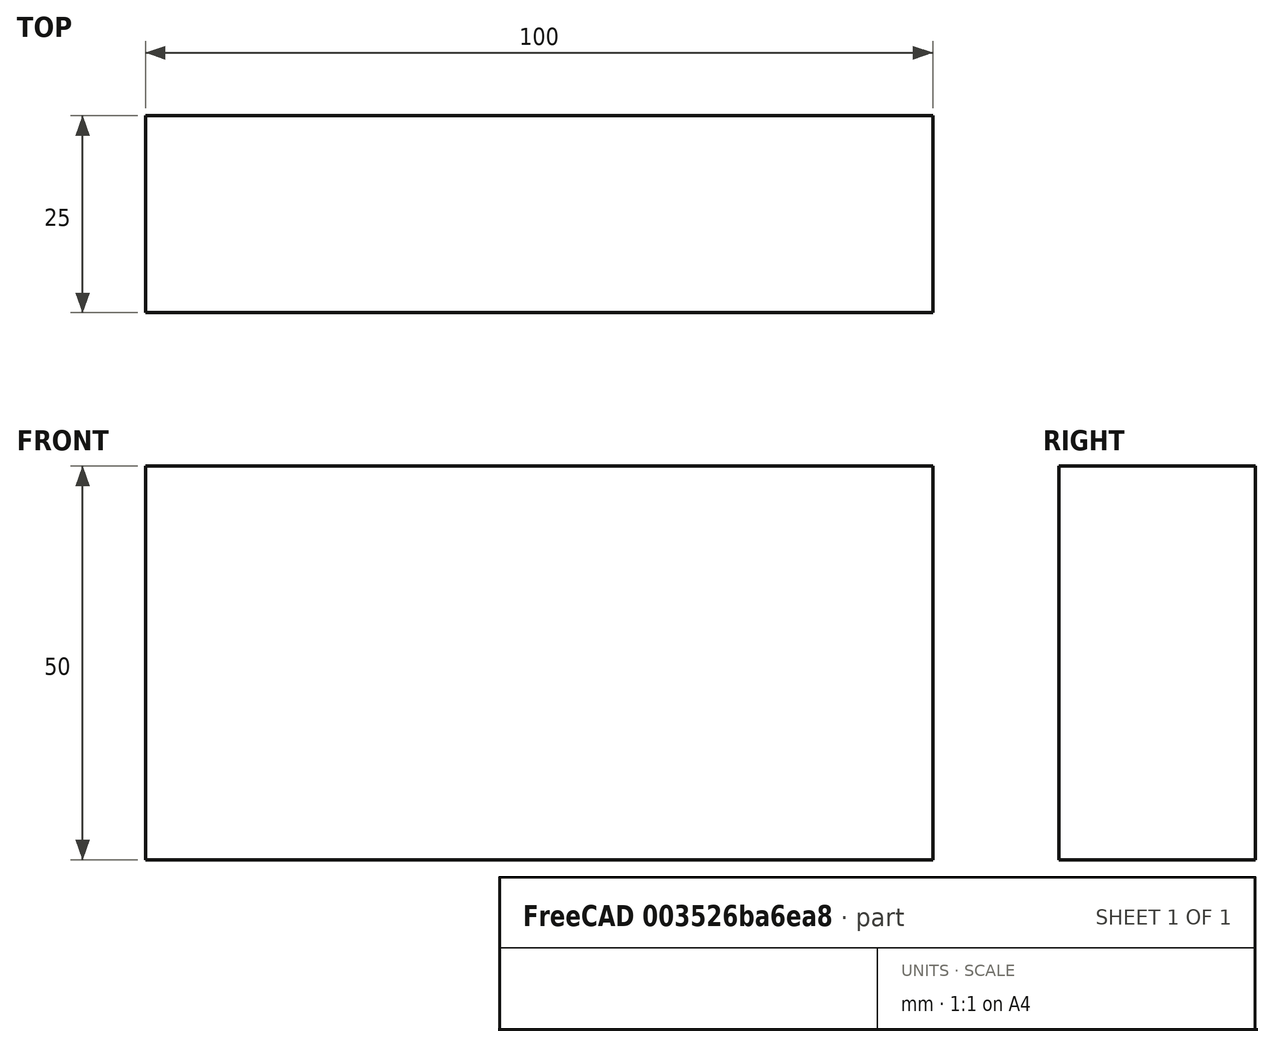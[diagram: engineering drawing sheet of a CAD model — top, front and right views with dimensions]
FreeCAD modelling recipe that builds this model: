
FCSTD DOCUMENT  (FreeCAD 0.15R4671 (Git))
Label: Flat Bar 100x25 EN10058 S235JR
License: All rights reserved
LicenseURL: http://en.wikipedia.org/wiki/All_rights_reserved
objects: Sketcher::SketchObject×1, Part::Extrusion×1
note: 2 computed .brp shape members not serialized (recipe doc carries the construction recipe); baked Part::Feature solids carry a one-line shape summary decoded from their .brp

FEATURE [Sketcher::SketchObject] Sketch
  sketch-geometry (4):
    g0: LineSegment StartX=-50 StartY=-12.5 StartZ=0 EndX=50 EndY=-12.5 EndZ=0
    g1: LineSegment StartX=50 StartY=-12.5 StartZ=0 EndX=50 EndY=12.5 EndZ=0
    g2: LineSegment StartX=50 StartY=12.5 StartZ=0 EndX=-50 EndY=12.5 EndZ=0
    g3: LineSegment StartX=-50 StartY=12.5 StartZ=0 EndX=-50 EndY=-12.5 EndZ=0
  constraints (12):
    c: Coincident(g0,g1)
    c: Coincident(g1,g2)
    c: Coincident(g2,g3)
    c: Coincident(g3,g0)
    c: Horizontal(g0)
    c: Horizontal(g2)
    c: Vertical(g1)
    c: Vertical(g3)
    c: Symmetric(g1,g2,g-2)
    c: Symmetric(g0,g1,g-1)
    c: DistanceY(g1) = 25
    c: DistanceX(g0) = 100
FEATURE [Part::Extrusion] Extrude  label="Flat Bar 100x25 EN10058 S235JR"
  Base = -> Sketch
  Dir = (0,0,50)
  Solid = true
